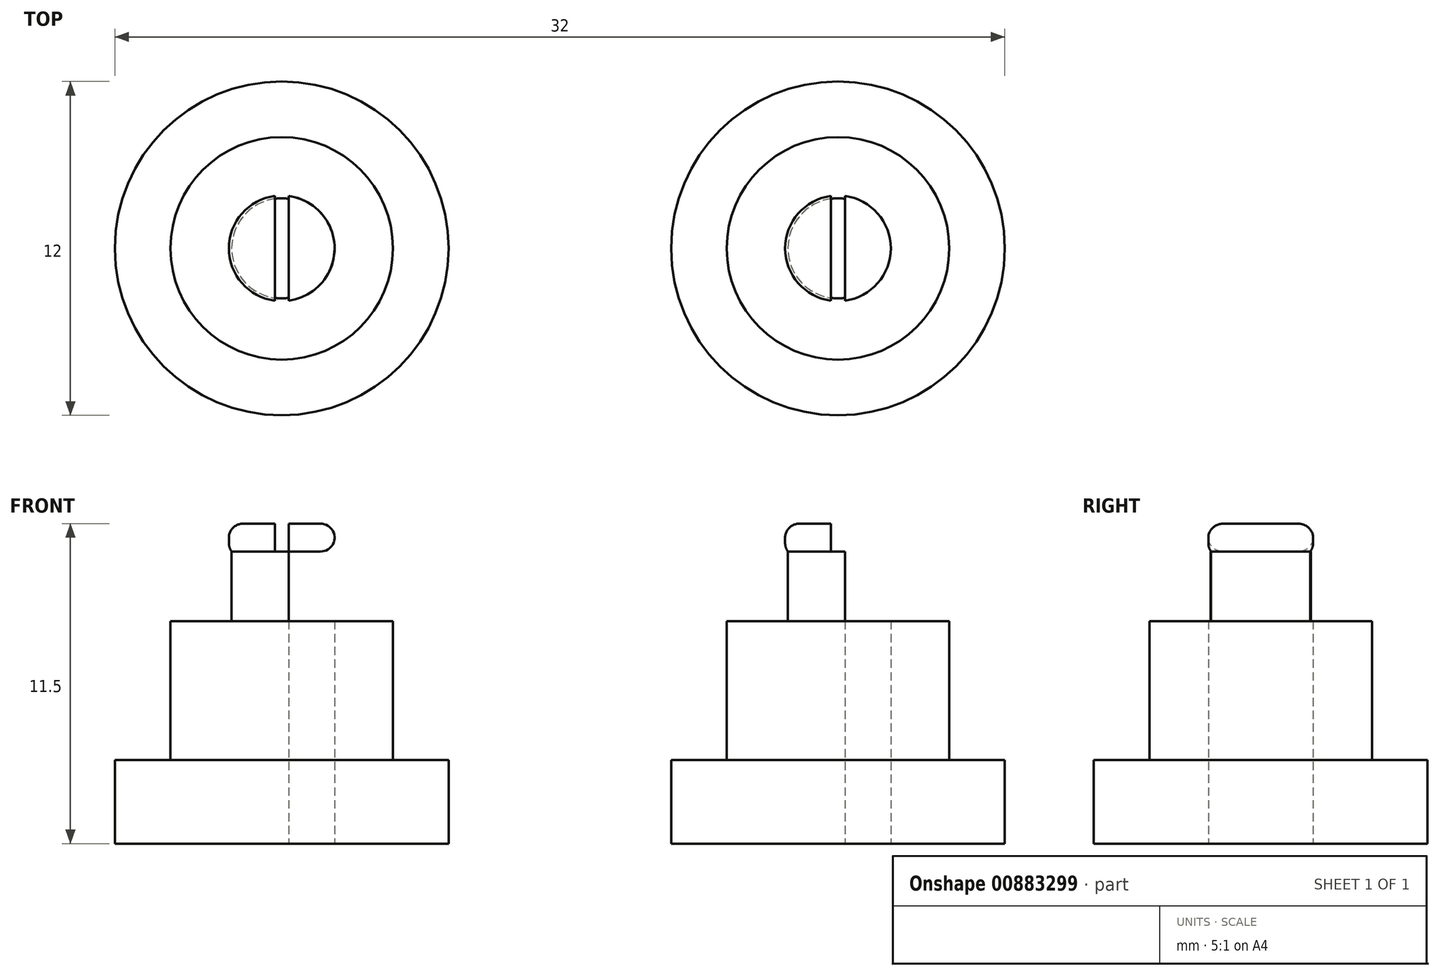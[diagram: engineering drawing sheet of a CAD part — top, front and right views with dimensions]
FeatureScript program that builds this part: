
annotation { "Feature Type Name" : "Feature", "Feature Type Description" : "" }
export const myFeature = defineFeature(function(context is Context, id is Id, definition is map)
    precondition{}
    {
        {
            var Q0;
            Q0=qCreatedBy(makeId("Top.planeOp"),FACE);
            var sketch = newSketch(context, id + "F0", { "sketchPlane" : qUnion([Q0])});
            skCircle(sketch, "E0", {"center": v(0, 0) * mm, "radius": 1.8 * mm});
            skCircle(sketch, "E1", {"center": v(0, 0) * mm, "radius": 4 * mm});
            skCircle(sketch, "E2", {"center": v(0, 0) * mm, "radius": 6 * mm});
            skCircle(sketch, "E3", {"center": v(0, 0) * mm, "radius": 1.9 * mm});
            skLineSegment(sketch, "E4.bottom", {"start": v(0.25, 2.5) * mm, "end": v(-0.25, 2.5) * mm});
            skLineSegment(sketch, "E4.top", {"start": v(0.25, -2.5) * mm, "end": v(-0.25, -2.5) * mm});
            skLineSegment(sketch, "E4.left", {"start": v(0.25, 2.5) * mm, "end": v(0.25, -2.5) * mm});
            skLineSegment(sketch, "E4.right", {"start": v(-0.25, 2.5) * mm, "end": v(-0.25, -2.5) * mm});
            skSolve(sketch);
        }
        {
            var Q0;
            {var subQ0=sQuery(id+"F0.wireOp",EDGE,"E4.right");var subQ1=sQuery(id+"F0.wireOp",EDGE,"E0");var subQ2=makeQuery(id+"F0.imprint","INTERSECT",VERTEX,{"disambiguationData":[OD(0.0)],"derivedFrom":[subQ1,subQ0]});Q0=makeQuery(id+"F0.imprint","IMPRINT",FACE,{"disambiguationData":[TD([[makeQuery(id+"F0.imprint","IMPRINT",EDGE,{"disambiguationData":[TD([[subQ2,-1.0]])],"derivedFrom":subQ1}),1.0]])]});}
            var Q1;
            {var subQ1=sQuery(id+"F0.wireOp",EDGE,"E0");var subQ3=makeQuery(id+"F0.imprint","IMPRINT",VERTEX,{"derivedFrom":subQ1});Q1=makeQuery(id+"F0.imprint","IMPRINT",FACE,{"disambiguationData":[TD([[makeQuery(id+"F0.imprint","IMPRINT",EDGE,{"disambiguationData":[TD([[subQ3,-1.0]])],"derivedFrom":subQ1}),1.0]])]});}
            var Q2;
            {var subQ0=sQuery(id+"F0.wireOp",EDGE,"E4.left");var subQ1=sQuery(id+"F0.wireOp",EDGE,"E0");var subQ2=makeQuery(id+"F0.imprint","INTERSECT",VERTEX,{"disambiguationData":[OD(0.0)],"derivedFrom":[subQ1,subQ0]});Q2=makeQuery(id+"F0.imprint","IMPRINT",FACE,{"disambiguationData":[TD([[makeQuery(id+"F0.imprint","IMPRINT",EDGE,{"disambiguationData":[TD([[subQ2,-1.0]])],"derivedFrom":subQ1}),1.0]])]});}
            extrude(context, id + "F1", {"entities" : qUnion([Q0, Q1, Q2]), "depth" : 10.5 * mm, "offsetDistance" : 25 * mm});
        }
        {
            var Q0;
            Q0=makeQuery(id+"F0.imprint","IMPRINT",FACE,{"disambiguationData":[TD([[makeQuery(id+"F0.imprint","IMPRINT",EDGE,{"derivedFrom":sQuery(id+"F0.wireOp",EDGE,"E1")}),1.0]])]});
            var Q1;
            {var subQ0=sQuery(id+"F0.wireOp",EDGE,"E4.right");var subQ1=sQuery(id+"F0.wireOp",EDGE,"E0");var subQ2=makeQuery(id+"F0.imprint","INTERSECT",VERTEX,{"disambiguationData":[OD(0.0)],"derivedFrom":[subQ1,subQ0]});Q1=makeQuery(id+"F0.imprint","IMPRINT",FACE,{"disambiguationData":[TD([[makeQuery(id+"F0.imprint","IMPRINT",EDGE,{"disambiguationData":[TD([[subQ2,-1.0]])],"derivedFrom":subQ1}),-1.0]])]});}
            var Q2;
            {var subQ0=sQuery(id+"F0.wireOp",EDGE,"E4.left");var subQ1=sQuery(id+"F0.wireOp",EDGE,"E0");var subQ2=makeQuery(id+"F0.imprint","INTERSECT",VERTEX,{"disambiguationData":[OD(0.0)],"derivedFrom":[subQ1,subQ0]});Q2=makeQuery(id+"F0.imprint","IMPRINT",FACE,{"disambiguationData":[TD([[makeQuery(id+"F0.imprint","IMPRINT",EDGE,{"disambiguationData":[TD([[subQ2,-1.0]])],"derivedFrom":subQ1}),1.0]])]});}
            var Q3;
            {var subQ4=sQuery(id+"F0.wireOp",EDGE,"E0");var subQ6=makeQuery(id+"F0.imprint","IMPRINT",VERTEX,{"derivedFrom":subQ4});Q3=makeQuery(id+"F0.imprint","IMPRINT",FACE,{"disambiguationData":[TD([[makeQuery(id+"F0.imprint","IMPRINT",EDGE,{"disambiguationData":[TD([[subQ6,-1.0]])],"derivedFrom":subQ4}),-1.0]])]});}
            var Q4;
            {var subQ5=sQuery(id+"F0.wireOp",EDGE,"E4.bottom");Q4=makeQuery(id+"F0.imprint","IMPRINT",FACE,{"disambiguationData":[TD([[makeQuery(id+"F0.imprint","IMPRINT",EDGE,{"derivedFrom":subQ5}),1.0]])]});}
            var Q5;
            {var subQ0=sQuery(id+"F0.wireOp",EDGE,"E4.left");var subQ1=sQuery(id+"F0.wireOp",EDGE,"E0");var subQ2=makeQuery(id+"F0.imprint","INTERSECT",VERTEX,{"disambiguationData":[OD(0.0)],"derivedFrom":[subQ1,subQ0]});Q5=makeQuery(id+"F0.imprint","IMPRINT",FACE,{"disambiguationData":[TD([[makeQuery(id+"F0.imprint","IMPRINT",EDGE,{"disambiguationData":[TD([[subQ2,-1.0]])],"derivedFrom":subQ1}),-1.0]])]});}
            var Q6;
            {var subQ0=sQuery(id+"F0.wireOp",EDGE,"E4.right");var subQ1=sQuery(id+"F0.wireOp",EDGE,"E0");var subQ2=makeQuery(id+"F0.imprint","INTERSECT",VERTEX,{"disambiguationData":[OD(1.0)],"derivedFrom":[subQ1,subQ0]});Q6=makeQuery(id+"F0.imprint","IMPRINT",FACE,{"disambiguationData":[TD([[makeQuery(id+"F0.imprint","IMPRINT",EDGE,{"disambiguationData":[TD([[subQ2,-1.0]])],"derivedFrom":subQ1}),-1.0]])]});}
            var Q7;
            {var subQ5=sQuery(id+"F0.wireOp",EDGE,"E4.top");Q7=makeQuery(id+"F0.imprint","IMPRINT",FACE,{"disambiguationData":[TD([[makeQuery(id+"F0.imprint","IMPRINT",EDGE,{"derivedFrom":subQ5}),-1.0]])]});}
            extrude(context, id + "F2", {"entities" : qUnion([Q0, Q1, Q2, Q3, Q4, Q5, Q6, Q7]), "operationType" : NewBodyOperationType.ADD, "depth" : 8 * mm, "offsetDistance" : 25 * mm});
        }
        {
            var Q0;
            Q0=makeQuery(id+"F0.imprint","IMPRINT",FACE,{"disambiguationData":[TD([[makeQuery(id+"F0.imprint","IMPRINT",EDGE,{"derivedFrom":sQuery(id+"F0.wireOp",EDGE,"E1")}),-1.0]])]});
            extrude(context, id + "F3", {"entities" : qUnion([Q0]), "operationType" : NewBodyOperationType.ADD, "depth" : 3 * mm, "offsetDistance" : 25 * mm});
        }
        {
            var Q0;
            Q0=makeQuery(id+"F2.opExtrude","CAP_FACE",FACE,{"disambiguationData":[OSD([sQuery(id+"F0.wireOp",EDGE,"E0"),sQuery(id+"F0.wireOp",EDGE,"E1"),sQuery(id+"F0.wireOp",EDGE,"E4.left"),sQuery(id+"F0.wireOp",EDGE,"E4.right")])],"isStart":false});
            cPlane(context, id + "F4", {"entities" : qUnion([Q0]), "cplaneType" : CPlaneType.OFFSET, "offset" : 2.5 * mm, "width" : 150 * mm, "height" : 150 * mm});
        }
        {
            var Q0;
            Q0=qCreatedBy(id+"F4.planeOp",FACE);
            var sketch = newSketch(context, id + "F5", { "sketchPlane" : qUnion([Q0])});
            skCircle(sketch, "E5.0", {"center": v(0, 0) * mm, "radius": 1.9 * mm});
            skLineSegment(sketch, "E6.0", {"start": v(0.25, 2.5) * mm, "end": v(0.25, -2.5) * mm});
            skLineSegment(sketch, "E6.1", {"start": v(0.25, 2.5) * mm, "end": v(-0.25, 2.5) * mm});
            skLineSegment(sketch, "E6.2", {"start": v(-0.25, 2.5) * mm, "end": v(-0.25, -2.5) * mm});
            skLineSegment(sketch, "E6.3", {"start": v(0.25, -2.5) * mm, "end": v(-0.25, -2.5) * mm});
            skSolve(sketch);
        }
        {
            var Q0;
            {var subQ0=sQuery(id+"F5.wireOp",EDGE,"E6.0");var subQ1=sQuery(id+"F5.wireOp",EDGE,"E5.0");var subQ2=makeQuery(id+"F5.imprint","INTERSECT",VERTEX,{"disambiguationData":[OD(0.0)],"derivedFrom":[subQ1,subQ0]});Q0=makeQuery(id+"F5.imprint","IMPRINT",FACE,{"disambiguationData":[TD([[makeQuery(id+"F5.imprint","IMPRINT",EDGE,{"disambiguationData":[TD([[subQ2,1.0]])],"derivedFrom":subQ1}),1.0]])]});}
            var Q1;
            {var subQ0=sQuery(id+"F5.wireOp",EDGE,"E6.2");var subQ1=sQuery(id+"F5.wireOp",EDGE,"E5.0");var subQ2=makeQuery(id+"F5.imprint","INTERSECT",VERTEX,{"disambiguationData":[OD(0.0)],"derivedFrom":[subQ1,subQ0]});Q1=makeQuery(id+"F5.imprint","IMPRINT",FACE,{"disambiguationData":[TD([[makeQuery(id+"F5.imprint","IMPRINT",EDGE,{"disambiguationData":[TD([[subQ2,-1.0]])],"derivedFrom":subQ1}),1.0]])]});}
            extrude(context, id + "F6", {"entities" : qUnion([Q0, Q1]), "operationType" : NewBodyOperationType.ADD, "depth" : 1 * mm, "offsetDistance" : 25 * mm});
        }
        {
            var Q0;
            {var subQ0=sQuery(id+"F5.wireOp",EDGE,"E6.0");var subQ1=sQuery(id+"F5.wireOp",EDGE,"E5.0");Q0=makeQuery(id+"F6.opExtrude","CAP_EDGE",EDGE,{"disambiguationData":[OSD([subQ1]),TDD([makeQuery(id+"F5.imprint","IMPRINT",EDGE,{"disambiguationData":[TD([[makeQuery(id+"F5.imprint","INTERSECT",VERTEX,{"disambiguationData":[OD(0.0)],"derivedFrom":[subQ1,subQ0]}),1.0]])],"derivedFrom":subQ1})])],"isStart":false});}
            var Q1;
            {var subQ0=sQuery(id+"F5.wireOp",EDGE,"E6.0");var subQ1=sQuery(id+"F5.wireOp",EDGE,"E5.0");Q1=makeQuery(id+"F6.opExtrude","CAP_EDGE",EDGE,{"disambiguationData":[OSD([subQ1]),TDD([makeQuery(id+"F5.imprint","IMPRINT",EDGE,{"disambiguationData":[TD([[makeQuery(id+"F5.imprint","INTERSECT",VERTEX,{"disambiguationData":[OD(0.0)],"derivedFrom":[subQ1,subQ0]}),1.0]])],"derivedFrom":subQ1})])],"isStart":true});}
            var Q2;
            {var subQ0=sQuery(id+"F5.wireOp",EDGE,"E6.2");var subQ1=sQuery(id+"F5.wireOp",EDGE,"E5.0");Q2=makeQuery(id+"F6.opExtrude","CAP_EDGE",EDGE,{"disambiguationData":[OSD([subQ1]),TDD([makeQuery(id+"F5.imprint","IMPRINT",EDGE,{"disambiguationData":[TD([[makeQuery(id+"F5.imprint","INTERSECT",VERTEX,{"disambiguationData":[OD(0.0)],"derivedFrom":[subQ1,subQ0]}),-1.0]])],"derivedFrom":subQ1})])],"isStart":true});}
            var Q3;
            {var subQ0=sQuery(id+"F5.wireOp",EDGE,"E6.2");var subQ1=sQuery(id+"F5.wireOp",EDGE,"E5.0");Q3=makeQuery(id+"F6.opExtrude","CAP_EDGE",EDGE,{"disambiguationData":[OSD([subQ1]),TDD([makeQuery(id+"F5.imprint","IMPRINT",EDGE,{"disambiguationData":[TD([[makeQuery(id+"F5.imprint","INTERSECT",VERTEX,{"disambiguationData":[OD(0.0)],"derivedFrom":[subQ1,subQ0]}),-1.0]])],"derivedFrom":subQ1})])],"isStart":false});}
            fillet(context, id + "F7", {"entities" : qUnion([Q0, Q1, Q2, Q3]), "tangentPropagation" : true, "radius" : 0.5 * mm, "defaultsChanged" : true, "vertexSettings" : [], "allowEdgeOverflow" : false});
        }
        {
            var Q0;
            Q0=makeQuery(id+"F1.opExtrude","SWEPT_BODY",BODY,{"disambiguationData":[OSD([sQuery(id+"F0.wireOp",EDGE,"E0"),sQuery(id+"F0.wireOp",EDGE,"E4.left")])]});
            transform(context, id + "F8", {"entities" : qUnion([Q0]), "transformType" : TransformType.TRANSLATION_3D, "dx" : 20 * mm, "dy" : 0 * mm, "dz" : 0 * mm, "makeCopy" : true});
        }
    });
